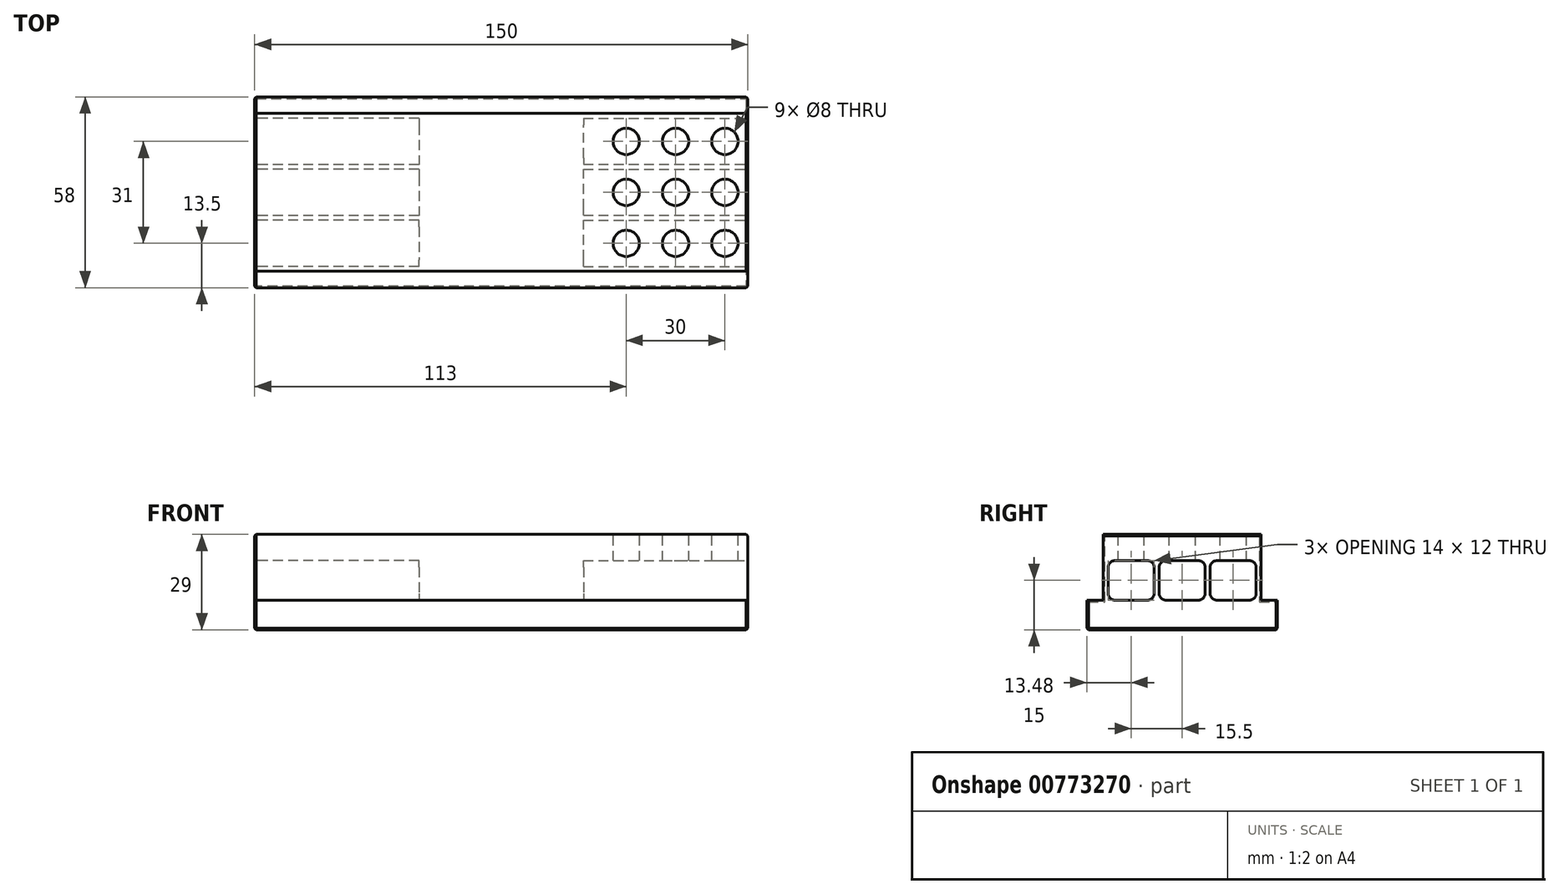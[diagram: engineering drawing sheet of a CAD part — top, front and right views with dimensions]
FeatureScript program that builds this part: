
annotation { "Feature Type Name" : "Feature", "Feature Type Description" : "" }
export const myFeature = defineFeature(function(context is Context, id is Id, definition is map)
    precondition{}
    {
        {
            var Q0;
            Q0=qCreatedBy(makeId("Top.planeOp"),FACE);
            var sketch = newSketch(context, id + "F0", { "sketchPlane" : qUnion([Q0])});
            skLineSegment(sketch, "E0.bottom", {"start": v(75, 29) * mm, "end": v(-75, 29) * mm});
            skLineSegment(sketch, "E0.top", {"start": v(75, -29) * mm, "end": v(-75, -29) * mm});
            skLineSegment(sketch, "E0.left", {"start": v(75, 29) * mm, "end": v(75, -29) * mm});
            skLineSegment(sketch, "E0.right", {"start": v(-75, 29) * mm, "end": v(-75, -29) * mm});
            skPoint(sketch, "E0.middle", {"position": v(0, 0) * mm});
            skSolve(sketch);
        }
        {
            var Q0;
            Q0 = qSketchRegion(id + "F0", true);
            extrude(context, id + "F1", {"entities" : qUnion([Q0]), "oppositeDirection" : true, "depth" : 29 * mm, "offsetDistance" : 25 * mm});
        }
        {
            var Q0;
            Q0=qCreatedBy(makeId("Top.planeOp"),FACE);
            var sketch = newSketch(context, id + "F2", { "sketchPlane" : qUnion([Q0])});
            skCircle(sketch, "E1", {"center": v(68, 15.5) * mm, "radius": 4 * mm});
            skCircle(sketch, "E2.0.1.0", {"center": v(68, 0) * mm, "radius": 4 * mm});
            skCircle(sketch, "E2.0.2.0", {"center": v(68, -15.5) * mm, "radius": 4 * mm});
            skCircle(sketch, "E2.1.0.0", {"center": v(53, 15.5) * mm, "radius": 4 * mm});
            skCircle(sketch, "E2.1.1.0", {"center": v(53, 0) * mm, "radius": 4 * mm});
            skCircle(sketch, "E2.1.2.0", {"center": v(53, -15.5) * mm, "radius": 4 * mm});
            skCircle(sketch, "E2.2.0.0", {"center": v(38, 15.5) * mm, "radius": 4 * mm});
            skCircle(sketch, "E2.2.1.0", {"center": v(38, 0) * mm, "radius": 4 * mm});
            skCircle(sketch, "E2.2.2.0", {"center": v(38, -15.5) * mm, "radius": 4 * mm});
            skLineSegment(sketch, "E2.direction1", {"start": v(68, 15.5) * mm, "end": v(53, 15.5) * mm, "construction": true});
            skLineSegment(sketch, "E2.direction2", {"start": v(68, 15.5) * mm, "end": v(68, 0) * mm, "construction": true});
            skLineSegment(sketch, "E3.MirrorCS", {"start": v(-68, 15.5) * mm, "end": v(-53, 15.5) * mm, "construction": true});
            skCircle(sketch, "E4.MirrorC", {"center": v(-53, 0) * mm, "radius": 4 * mm});
            skCircle(sketch, "E5.MirrorC", {"center": v(-53, 15.5) * mm, "radius": 4 * mm});
            skCircle(sketch, "E6.MirrorC", {"center": v(-53, -15.5) * mm, "radius": 4 * mm});
            skCircle(sketch, "E7.MirrorC", {"center": v(-68, 15.5) * mm, "radius": 4 * mm});
            skCircle(sketch, "E8.MirrorC", {"center": v(-38, 0) * mm, "radius": 4 * mm});
            skLineSegment(sketch, "E9.MirrorCS", {"start": v(-68, 15.5) * mm, "end": v(-68, 0) * mm, "construction": true});
            skCircle(sketch, "E10.MirrorC", {"center": v(-68, -15.5) * mm, "radius": 4 * mm});
            skCircle(sketch, "E11.MirrorC", {"center": v(-68, 0) * mm, "radius": 4 * mm});
            skCircle(sketch, "E12.MirrorC", {"center": v(-38, -15.5) * mm, "radius": 4 * mm});
            skCircle(sketch, "E13.MirrorC", {"center": v(-38, 15.5) * mm, "radius": 4 * mm});
            skSolve(sketch);
        }
        {
            var Q0;
            Q0=makeQuery(id+"F1.opExtrude","SWEPT_FACE",FACE,{"disambiguationData":[OSD([sQuery(id+"F0.wireOp",EDGE,"E0.left")])]});
            var sketch = newSketch(context, id + "F3", { "sketchPlane" : qUnion([Q0])});
            skLineSegment(sketch, "E14.bottom", {"start": v(-29, 0) * mm, "end": v(-24, 0) * mm});
            skLineSegment(sketch, "E14.top", {"start": v(-29, -20) * mm, "end": v(-24, -20) * mm});
            skLineSegment(sketch, "E14.left", {"start": v(-29, 0) * mm, "end": v(-29, -20) * mm});
            skLineSegment(sketch, "E14.right", {"start": v(-24, 0) * mm, "end": v(-24, -20) * mm});
            skLineSegment(sketch, "E15.bottom", {"start": v(29, 0) * mm, "end": v(24, 0) * mm});
            skLineSegment(sketch, "E15.top", {"start": v(29, -20) * mm, "end": v(24, -20) * mm});
            skLineSegment(sketch, "E15.left", {"start": v(29, 0) * mm, "end": v(29, -20) * mm});
            skLineSegment(sketch, "E15.right", {"start": v(24, 0) * mm, "end": v(24, -20) * mm});
            skSolve(sketch);
        }
        {
            var Q0;
            Q0=makeQuery(id+"F3.imprint","IMPRINT",FACE,{"disambiguationData":[TD([[makeQuery(id+"F3.imprint","IMPRINT",EDGE,{"derivedFrom":sQuery(id+"F3.wireOp",EDGE,"E14.bottom")}),1.0]])]});
            var Q1;
            Q1=makeQuery(id+"F3.imprint","IMPRINT",FACE,{"disambiguationData":[TD([[makeQuery(id+"F3.imprint","IMPRINT",EDGE,{"derivedFrom":sQuery(id+"F3.wireOp",EDGE,"E15.bottom")}),1.0]])]});
            extrude(context, id + "F4", {"entities" : qUnion([Q0, Q1]), "operationType" : NewBodyOperationType.REMOVE, "endBound" : BoundingType.THROUGH_ALL, "oppositeDirection" : true, "depth" : 25 * mm, "offsetDistance" : 25 * mm});
        }
        {
            var Q0;
            Q0=makeQuery(id+"F2.imprint","IMPRINT",FACE,{"disambiguationData":[TD([[makeQuery(id+"F2.imprint","IMPRINT",EDGE,{"derivedFrom":sQuery(id+"F2.wireOp",EDGE,"E1")}),1.0]])]});
            var Q1;
            Q1=makeQuery(id+"F2.imprint","IMPRINT",FACE,{"disambiguationData":[TD([[makeQuery(id+"F2.imprint","IMPRINT",EDGE,{"derivedFrom":sQuery(id+"F2.wireOp",EDGE,"E2.2.2.0")}),1.0]])]});
            var Q2;
            Q2=makeQuery(id+"F2.imprint","IMPRINT",FACE,{"disambiguationData":[TD([[makeQuery(id+"F2.imprint","IMPRINT",EDGE,{"derivedFrom":sQuery(id+"F2.wireOp",EDGE,"E2.2.0.0")}),1.0]])]});
            var Q3;
            Q3=makeQuery(id+"F2.imprint","IMPRINT",FACE,{"disambiguationData":[TD([[makeQuery(id+"F2.imprint","IMPRINT",EDGE,{"derivedFrom":sQuery(id+"F2.wireOp",EDGE,"E2.2.1.0")}),1.0]])]});
            var Q4;
            Q4=makeQuery(id+"F2.imprint","IMPRINT",FACE,{"disambiguationData":[TD([[makeQuery(id+"F2.imprint","IMPRINT",EDGE,{"derivedFrom":sQuery(id+"F2.wireOp",EDGE,"E2.0.1.0")}),1.0]])]});
            var Q5;
            Q5=makeQuery(id+"F2.imprint","IMPRINT",FACE,{"disambiguationData":[TD([[makeQuery(id+"F2.imprint","IMPRINT",EDGE,{"derivedFrom":sQuery(id+"F2.wireOp",EDGE,"E2.1.2.0")}),1.0]])]});
            var Q6;
            Q6=makeQuery(id+"F2.imprint","IMPRINT",FACE,{"disambiguationData":[TD([[makeQuery(id+"F2.imprint","IMPRINT",EDGE,{"derivedFrom":sQuery(id+"F2.wireOp",EDGE,"E2.0.2.0")}),1.0]])]});
            var Q7;
            Q7=makeQuery(id+"F2.imprint","IMPRINT",FACE,{"disambiguationData":[TD([[makeQuery(id+"F2.imprint","IMPRINT",EDGE,{"derivedFrom":sQuery(id+"F2.wireOp",EDGE,"E2.1.1.0")}),1.0]])]});
            var Q8;
            Q8=makeQuery(id+"F2.imprint","IMPRINT",FACE,{"disambiguationData":[TD([[makeQuery(id+"F2.imprint","IMPRINT",EDGE,{"derivedFrom":sQuery(id+"F2.wireOp",EDGE,"E2.1.0.0")}),1.0]])]});
            var Q9;
            Q9=makeQuery(id+"F2.imprint","IMPRINT",FACE,{"disambiguationData":[TD([[makeQuery(id+"F2.imprint","IMPRINT",EDGE,{"derivedFrom":sQuery(id+"F2.wireOp",EDGE,"E7.MirrorC")}),-1.0]])]});
            var Q10;
            Q10=makeQuery(id+"F2.imprint","IMPRINT",FACE,{"disambiguationData":[TD([[makeQuery(id+"F2.imprint","IMPRINT",EDGE,{"derivedFrom":sQuery(id+"F2.wireOp",EDGE,"E4.MirrorC")}),-1.0]])]});
            var Q11;
            Q11=makeQuery(id+"F2.imprint","IMPRINT",FACE,{"disambiguationData":[TD([[makeQuery(id+"F2.imprint","IMPRINT",EDGE,{"derivedFrom":sQuery(id+"F2.wireOp",EDGE,"E8.MirrorC")}),-1.0]])]});
            var Q12;
            Q12=makeQuery(id+"F2.imprint","IMPRINT",FACE,{"disambiguationData":[TD([[makeQuery(id+"F2.imprint","IMPRINT",EDGE,{"derivedFrom":sQuery(id+"F2.wireOp",EDGE,"E10.MirrorC")}),-1.0]])]});
            var Q13;
            Q13=makeQuery(id+"F2.imprint","IMPRINT",FACE,{"disambiguationData":[TD([[makeQuery(id+"F2.imprint","IMPRINT",EDGE,{"derivedFrom":sQuery(id+"F2.wireOp",EDGE,"E12.MirrorC")}),-1.0]])]});
            var Q14;
            Q14=makeQuery(id+"F2.imprint","IMPRINT",FACE,{"disambiguationData":[TD([[makeQuery(id+"F2.imprint","IMPRINT",EDGE,{"derivedFrom":sQuery(id+"F2.wireOp",EDGE,"E11.MirrorC")}),-1.0]])]});
            var Q15;
            Q15=makeQuery(id+"F2.imprint","IMPRINT",FACE,{"disambiguationData":[TD([[makeQuery(id+"F2.imprint","IMPRINT",EDGE,{"derivedFrom":sQuery(id+"F2.wireOp",EDGE,"E13.MirrorC")}),-1.0]])]});
            var Q16;
            Q16=makeQuery(id+"F2.imprint","IMPRINT",FACE,{"disambiguationData":[TD([[makeQuery(id+"F2.imprint","IMPRINT",EDGE,{"derivedFrom":sQuery(id+"F2.wireOp",EDGE,"E5.MirrorC")}),-1.0]])]});
            var Q17;
            Q17=makeQuery(id+"F2.imprint","IMPRINT",FACE,{"disambiguationData":[TD([[makeQuery(id+"F2.imprint","IMPRINT",EDGE,{"derivedFrom":sQuery(id+"F2.wireOp",EDGE,"E6.MirrorC")}),-1.0]])]});
            extrude(context, id + "F5", {"entities" : qUnion([Q0, Q1, Q2, Q3, Q4, Q5, Q6, Q7, Q8, Q9, Q10, Q11, Q12, Q13, Q14, Q15, Q16, Q17]), "operationType" : NewBodyOperationType.REMOVE, "oppositeDirection" : true, "depth" : 20 * mm, "offsetDistance" : 25 * mm});
        }
        {
            var Q0;
            Q0=makeQuery(id+"F1.opExtrude","SWEPT_FACE",FACE,{"disambiguationData":[OSD([sQuery(id+"F0.wireOp",EDGE,"E0.left")])]});
            var sketch = newSketch(context, id + "F6", { "sketchPlane" : qUnion([Q0])});
            skLineSegment(sketch, "E16.bottom", {"start": v(-20.5, -8) * mm, "end": v(-10.5, -8) * mm});
            skLineSegment(sketch, "E16.top", {"start": v(-20.5, -20) * mm, "end": v(-10.5, -20) * mm});
            skLineSegment(sketch, "E16.left", {"start": v(-22.5, -10) * mm, "end": v(-22.5, -18) * mm});
            skLineSegment(sketch, "E16.right", {"start": v(-8.5, -10) * mm, "end": v(-8.5, -18) * mm});
            skLineSegment(sketch, "E17.1.0.0", {"start": v(7, -10) * mm, "end": v(7, -18) * mm});
            skLineSegment(sketch, "E17.1.0.1", {"start": v(-5, -8) * mm, "end": v(5, -8) * mm});
            skLineSegment(sketch, "E17.1.0.2", {"start": v(-7, -10) * mm, "end": v(-7, -18) * mm});
            skLineSegment(sketch, "E17.1.0.3", {"start": v(-5, -20) * mm, "end": v(5, -20) * mm});
            skLineSegment(sketch, "E17.2.0.0", {"start": v(22.5, -10) * mm, "end": v(22.5, -18) * mm});
            skLineSegment(sketch, "E17.2.0.1", {"start": v(10.5, -8) * mm, "end": v(20.5, -8) * mm});
            skLineSegment(sketch, "E17.2.0.2", {"start": v(8.5, -10) * mm, "end": v(8.5, -18) * mm});
            skLineSegment(sketch, "E17.2.0.3", {"start": v(10.5, -20) * mm, "end": v(20.5, -20) * mm});
            skLineSegment(sketch, "E17.direction1", {"start": v(-8.5, -20) * mm, "end": v(7, -20) * mm, "construction": true});
            skLineSegment(sketch, "E18", {"start": v(0, -8) * mm, "end": v(0, -20) * mm, "construction": true});
            skPoint(sketch, "E19.visualSharp", {"position": v(-22.5, -8) * mm});
            skArc(sketch, "E19.filletArc", {"start": v(-20.5, -8) * mm, "mid": v(-21.91, -8.59) * mm, "end": v(-22.5, -10) * mm});
            skPoint(sketch, "E20.visualSharp", {"position": v(-22.5, -20) * mm});
            skArc(sketch, "E20.filletArc", {"start": v(-22.5, -18) * mm, "mid": v(-21.91, -19.41) * mm, "end": v(-20.5, -20) * mm});
            skPoint(sketch, "E21.visualSharp", {"position": v(-8.5, -20) * mm});
            skArc(sketch, "E21.filletArc", {"start": v(-10.5, -20) * mm, "mid": v(-9.09, -19.41) * mm, "end": v(-8.5, -18) * mm});
            skPoint(sketch, "E22.visualSharp", {"position": v(-8.5, -8) * mm});
            skArc(sketch, "E22.filletArc", {"start": v(-8.5, -10) * mm, "mid": v(-9.09, -8.59) * mm, "end": v(-10.5, -8) * mm});
            skPoint(sketch, "E23.visualSharp", {"position": v(-7, -8) * mm});
            skArc(sketch, "E23.filletArc", {"start": v(-5, -8) * mm, "mid": v(-6.41, -8.59) * mm, "end": v(-7, -10) * mm});
            skPoint(sketch, "E24.visualSharp", {"position": v(-7, -20) * mm});
            skArc(sketch, "E24.filletArc", {"start": v(-7, -18) * mm, "mid": v(-6.41, -19.41) * mm, "end": v(-5, -20) * mm});
            skPoint(sketch, "E25.visualSharp", {"position": v(7, -20) * mm});
            skArc(sketch, "E25.filletArc", {"start": v(5, -20) * mm, "mid": v(6.41, -19.41) * mm, "end": v(7, -18) * mm});
            skPoint(sketch, "E26.visualSharp", {"position": v(7, -8) * mm});
            skArc(sketch, "E26.filletArc", {"start": v(7, -10) * mm, "mid": v(6.41, -8.59) * mm, "end": v(5, -8) * mm});
            skPoint(sketch, "E27.visualSharp", {"position": v(8.5, -8) * mm});
            skArc(sketch, "E27.filletArc", {"start": v(10.5, -8) * mm, "mid": v(9.09, -8.59) * mm, "end": v(8.5, -10) * mm});
            skPoint(sketch, "E28.visualSharp", {"position": v(22.5, -20) * mm});
            skArc(sketch, "E28.filletArc", {"start": v(20.5, -20) * mm, "mid": v(21.91, -19.41) * mm, "end": v(22.5, -18) * mm});
            skPoint(sketch, "E29.visualSharp", {"position": v(22.5, -8) * mm});
            skArc(sketch, "E29.filletArc", {"start": v(22.5, -10) * mm, "mid": v(21.91, -8.59) * mm, "end": v(20.5, -8) * mm});
            skPoint(sketch, "E30.visualSharp", {"position": v(8.5, -20) * mm});
            skArc(sketch, "E30.filletArc", {"start": v(8.5, -18) * mm, "mid": v(9.09, -19.41) * mm, "end": v(10.5, -20) * mm});
            skSolve(sketch);
        }
        {
            var Q0;
            Q0=makeQuery(id+"F1.opExtrude","SWEPT_FACE",FACE,{"disambiguationData":[OSD([sQuery(id+"F0.wireOp",EDGE,"E0.right")])]});
            var sketch = newSketch(context, id + "F7", { "sketchPlane" : qUnion([Q0])});
            skLineSegment(sketch, "E31.bottom", {"start": v(-20.48, -8) * mm, "end": v(-10.48, -8) * mm});
            skLineSegment(sketch, "E31.top", {"start": v(-20.48, -20) * mm, "end": v(-10.48, -20) * mm});
            skLineSegment(sketch, "E31.left", {"start": v(-22.48, -10) * mm, "end": v(-22.48, -18) * mm});
            skLineSegment(sketch, "E31.right", {"start": v(-8.48, -10) * mm, "end": v(-8.48, -18) * mm});
            skLineSegment(sketch, "E32.1.0.0", {"start": v(7.02, -10) * mm, "end": v(7.02, -18) * mm});
            skLineSegment(sketch, "E32.1.0.1", {"start": v(-4.98, -8) * mm, "end": v(5.02, -8) * mm});
            skLineSegment(sketch, "E32.1.0.2", {"start": v(-6.98, -10) * mm, "end": v(-6.98, -18) * mm});
            skLineSegment(sketch, "E32.1.0.3", {"start": v(-4.98, -20) * mm, "end": v(5.02, -20) * mm});
            skLineSegment(sketch, "E32.2.0.0", {"start": v(22.52, -10) * mm, "end": v(22.52, -18) * mm});
            skLineSegment(sketch, "E32.2.0.1", {"start": v(10.52, -8) * mm, "end": v(20.52, -8) * mm});
            skLineSegment(sketch, "E32.2.0.2", {"start": v(8.52, -10) * mm, "end": v(8.52, -18) * mm});
            skLineSegment(sketch, "E32.2.0.3", {"start": v(10.52, -20) * mm, "end": v(20.52, -20) * mm});
            skLineSegment(sketch, "E32.direction1", {"start": v(-8.48, -20) * mm, "end": v(7.02, -20) * mm, "construction": true});
            skLineSegment(sketch, "E33", {"start": v(0.02, -8) * mm, "end": v(0.02, -20) * mm, "construction": true});
            skPoint(sketch, "E34.visualSharp", {"position": v(-22.48, -8) * mm});
            skArc(sketch, "E34.filletArc", {"start": v(-20.48, -8) * mm, "mid": v(-21.9, -8.59) * mm, "end": v(-22.48, -10) * mm});
            skPoint(sketch, "E35.visualSharp", {"position": v(-22.48, -20) * mm});
            skArc(sketch, "E35.filletArc", {"start": v(-22.48, -18) * mm, "mid": v(-21.9, -19.41) * mm, "end": v(-20.48, -20) * mm});
            skPoint(sketch, "E36.visualSharp", {"position": v(-8.48, -20) * mm});
            skArc(sketch, "E36.filletArc", {"start": v(-10.48, -20) * mm, "mid": v(-9.07, -19.41) * mm, "end": v(-8.48, -18) * mm});
            skPoint(sketch, "E37.visualSharp", {"position": v(-8.48, -8) * mm});
            skArc(sketch, "E37.filletArc", {"start": v(-8.48, -10) * mm, "mid": v(-9.07, -8.59) * mm, "end": v(-10.48, -8) * mm});
            skPoint(sketch, "E38.visualSharp", {"position": v(-6.98, -8) * mm});
            skArc(sketch, "E38.filletArc", {"start": v(-4.98, -8) * mm, "mid": v(-6.4, -8.59) * mm, "end": v(-6.98, -10) * mm});
            skPoint(sketch, "E39.visualSharp", {"position": v(-6.98, -20) * mm});
            skArc(sketch, "E39.filletArc", {"start": v(-6.98, -18) * mm, "mid": v(-6.4, -19.41) * mm, "end": v(-4.98, -20) * mm});
            skPoint(sketch, "E40.visualSharp", {"position": v(7.02, -20) * mm});
            skArc(sketch, "E40.filletArc", {"start": v(5.02, -20) * mm, "mid": v(6.43, -19.41) * mm, "end": v(7.02, -18) * mm});
            skPoint(sketch, "E41.visualSharp", {"position": v(7.02, -8) * mm});
            skArc(sketch, "E41.filletArc", {"start": v(7.02, -10) * mm, "mid": v(6.43, -8.59) * mm, "end": v(5.02, -8) * mm});
            skPoint(sketch, "E42.visualSharp", {"position": v(8.52, -8) * mm});
            skArc(sketch, "E42.filletArc", {"start": v(10.52, -8) * mm, "mid": v(9.1, -8.59) * mm, "end": v(8.52, -10) * mm});
            skPoint(sketch, "E43.visualSharp", {"position": v(22.52, -20) * mm});
            skArc(sketch, "E43.filletArc", {"start": v(20.52, -20) * mm, "mid": v(21.93, -19.41) * mm, "end": v(22.52, -18) * mm});
            skPoint(sketch, "E44.visualSharp", {"position": v(22.52, -8) * mm});
            skArc(sketch, "E44.filletArc", {"start": v(22.52, -10) * mm, "mid": v(21.93, -8.59) * mm, "end": v(20.52, -8) * mm});
            skPoint(sketch, "E45.visualSharp", {"position": v(8.52, -20) * mm});
            skArc(sketch, "E45.filletArc", {"start": v(8.52, -18) * mm, "mid": v(9.1, -19.41) * mm, "end": v(10.52, -20) * mm});
            skSolve(sketch);
        }
        {
            var Q0;
            Q0=makeQuery(id+"F6.imprint","IMPRINT",FACE,{"disambiguationData":[TD([[makeQuery(id+"F6.imprint","IMPRINT",EDGE,{"derivedFrom":sQuery(id+"F6.wireOp",EDGE,"E16.bottom")}),-1.0]])]});
            var Q1;
            Q1=makeQuery(id+"F6.imprint","IMPRINT",FACE,{"disambiguationData":[TD([[makeQuery(id+"F6.imprint","IMPRINT",EDGE,{"derivedFrom":sQuery(id+"F6.wireOp",EDGE,"E17.1.0.0")}),-1.0]])]});
            var Q2;
            Q2=makeQuery(id+"F6.imprint","IMPRINT",FACE,{"disambiguationData":[TD([[makeQuery(id+"F6.imprint","IMPRINT",EDGE,{"derivedFrom":sQuery(id+"F6.wireOp",EDGE,"E17.2.0.0")}),-1.0]])]});
            extrude(context, id + "F8", {"entities" : qUnion([Q0, Q1, Q2]), "operationType" : NewBodyOperationType.REMOVE, "oppositeDirection" : true, "depth" : 50 * mm, "offsetDistance" : 25 * mm});
        }
        {
            var Q0;
            Q0=makeQuery(id+"F7.imprint","IMPRINT",FACE,{"disambiguationData":[TD([[makeQuery(id+"F7.imprint","IMPRINT",EDGE,{"derivedFrom":sQuery(id+"F7.wireOp",EDGE,"E31.bottom")}),-1.0]])]});
            var Q1;
            Q1=makeQuery(id+"F7.imprint","IMPRINT",FACE,{"disambiguationData":[TD([[makeQuery(id+"F7.imprint","IMPRINT",EDGE,{"derivedFrom":sQuery(id+"F7.wireOp",EDGE,"E32.1.0.0")}),-1.0]])]});
            var Q2;
            Q2=makeQuery(id+"F7.imprint","IMPRINT",FACE,{"disambiguationData":[TD([[makeQuery(id+"F7.imprint","IMPRINT",EDGE,{"derivedFrom":sQuery(id+"F7.wireOp",EDGE,"E32.2.0.0")}),-1.0]])]});
            extrude(context, id + "F9", {"entities" : qUnion([Q0, Q1, Q2]), "operationType" : NewBodyOperationType.REMOVE, "oppositeDirection" : true, "depth" : 50 * mm, "offsetDistance" : 25 * mm});
        }
        {
            var Q0;
            Q0=makeQuery(id+"F8.boolean.opBoolean","COPY",EDGE,{"derivedFrom":makeQuery(id+"F8.opExtrude","CAP_EDGE",EDGE,{"disambiguationData":[OSD([sQuery(id+"F6.wireOp",EDGE,"E16.bottom")])],"isStart":true})});
            var Q1;
            Q1=makeQuery(id+"F8.boolean.opBoolean","COPY",EDGE,{"derivedFrom":makeQuery(id+"F8.opExtrude","CAP_EDGE",EDGE,{"disambiguationData":[OSD([sQuery(id+"F6.wireOp",EDGE,"E17.1.0.1")])],"isStart":true})});
            var Q2;
            Q2=makeQuery(id+"F8.boolean.opBoolean","COPY",EDGE,{"derivedFrom":makeQuery(id+"F8.opExtrude","CAP_EDGE",EDGE,{"disambiguationData":[OSD([sQuery(id+"F6.wireOp",EDGE,"E17.2.0.1")])],"isStart":true})});
            var Q3;
            Q3=makeQuery(id+"F9.boolean.opBoolean","COPY",EDGE,{"derivedFrom":makeQuery(id+"F9.opExtrude","CAP_EDGE",EDGE,{"disambiguationData":[OSD([sQuery(id+"F7.wireOp",EDGE,"E31.bottom")])],"isStart":true})});
            var Q4;
            Q4=makeQuery(id+"F9.boolean.opBoolean","COPY",EDGE,{"derivedFrom":makeQuery(id+"F9.opExtrude","CAP_EDGE",EDGE,{"disambiguationData":[OSD([sQuery(id+"F7.wireOp",EDGE,"E32.1.0.1")])],"isStart":true})});
            var Q5;
            Q5=makeQuery(id+"F9.boolean.opBoolean","COPY",EDGE,{"derivedFrom":makeQuery(id+"F9.opExtrude","CAP_EDGE",EDGE,{"disambiguationData":[OSD([sQuery(id+"F7.wireOp",EDGE,"E32.2.0.1")])],"isStart":true})});
            var Q6;
            Q6=makeQuery(id+"F4.boolean.opBoolean","COPY",EDGE,{"derivedFrom":makeQuery(id+"F4.opExtrude","CAP_EDGE",EDGE,{"disambiguationData":[OSD([sQuery(id+"F3.wireOp",EDGE,"E14.right")])],"isStart":true})});
            var Q7;
            Q7=makeQuery(id+"F1.opExtrude","CAP_EDGE",EDGE,{"disambiguationData":[OSD([sQuery(id+"F0.wireOp",EDGE,"E0.left")])],"isStart":true});
            var Q8;
            Q8=makeQuery(id+"F4.boolean.opBoolean","COPY",EDGE,{"derivedFrom":makeQuery(id+"F4.opExtrude","CAP_EDGE",EDGE,{"disambiguationData":[OSD([sQuery(id+"F3.wireOp",EDGE,"E15.right")])],"isStart":true})});
            var Q9;
            Q9=makeQuery(id+"F4.boolean.opBoolean","COPY",EDGE,{"derivedFrom":makeQuery(id+"F4.opExtrude","SWEPT_EDGE",EDGE,{"disambiguationData":[OSD([sQuery(id+"F0.wireOp",EDGE,"E0.left"),sQuery(id+"F3.wireOp",EDGE,"E14.bottom"),sQuery(id+"F3.wireOp",EDGE,"E14.right")])]})});
            var Q10;
            Q10=makeQuery(id+"F4.boolean.opBoolean","COPY",EDGE,{"derivedFrom":makeQuery(id+"F4.opExtrude","SWEPT_EDGE",EDGE,{"disambiguationData":[OSD([sQuery(id+"F0.wireOp",EDGE,"E0.left"),sQuery(id+"F3.wireOp",EDGE,"E15.bottom"),sQuery(id+"F3.wireOp",EDGE,"E15.right")])]})});
            var Q11;
            Q11=makeQuery(id+"F1.opExtrude","CAP_EDGE",EDGE,{"disambiguationData":[OSD([sQuery(id+"F0.wireOp",EDGE,"E0.right")])],"isStart":true});
            var Q12;
            Q12=makeQuery(id+"F4.boolean.opBoolean","INTERSECT",EDGE,{"derivedFrom":[makeQuery(id+"F1.opExtrude","SWEPT_FACE",FACE,{"disambiguationData":[OSD([sQuery(id+"F0.wireOp",EDGE,"E0.right")])]}),makeQuery(id+"F4.opExtrude","SWEPT_FACE",FACE,{"disambiguationData":[OSD([sQuery(id+"F3.wireOp",EDGE,"E15.right")])]})]});
            var Q13;
            Q13=makeQuery(id+"F4.boolean.opBoolean","INTERSECT",EDGE,{"derivedFrom":[makeQuery(id+"F1.opExtrude","SWEPT_FACE",FACE,{"disambiguationData":[OSD([sQuery(id+"F0.wireOp",EDGE,"E0.right")])]}),makeQuery(id+"F4.opExtrude","SWEPT_FACE",FACE,{"disambiguationData":[OSD([sQuery(id+"F3.wireOp",EDGE,"E14.right")])]})]});
            var Q14;
            Q14=makeQuery(id+"F4.boolean.opBoolean","COPY",EDGE,{"derivedFrom":makeQuery(id+"F4.opExtrude","CAP_EDGE",EDGE,{"disambiguationData":[OSD([sQuery(id+"F3.wireOp",EDGE,"E14.top")])],"isStart":true})});
            var Q15;
            Q15=makeQuery(id+"F4.boolean.opBoolean","COPY",EDGE,{"derivedFrom":makeQuery(id+"F4.opExtrude","SWEPT_EDGE",EDGE,{"disambiguationData":[OSD([sQuery(id+"F0.wireOp",EDGE,"E0.top"),sQuery(id+"F0.wireOp",EDGE,"E0.left"),sQuery(id+"F3.wireOp",EDGE,"E14.top"),sQuery(id+"F3.wireOp",EDGE,"E14.left")])]})});
            var Q16;
            Q16=makeQuery(id+"F4.boolean.opBoolean","INTERSECT",EDGE,{"derivedFrom":[makeQuery(id+"F1.opExtrude","SWEPT_FACE",FACE,{"disambiguationData":[OSD([sQuery(id+"F0.wireOp",EDGE,"E0.right")])]}),makeQuery(id+"F4.opExtrude","SWEPT_FACE",FACE,{"disambiguationData":[OSD([sQuery(id+"F3.wireOp",EDGE,"E14.top")])]})]});
            var Q17;
            Q17=makeQuery(id+"F4.boolean.opBoolean","COPY",EDGE,{"derivedFrom":makeQuery(id+"F4.opExtrude","CAP_EDGE",EDGE,{"disambiguationData":[OSD([sQuery(id+"F3.wireOp",EDGE,"E15.top")])],"isStart":true})});
            var Q18;
            Q18=makeQuery(id+"F4.boolean.opBoolean","COPY",EDGE,{"derivedFrom":makeQuery(id+"F4.opExtrude","SWEPT_EDGE",EDGE,{"disambiguationData":[OSD([sQuery(id+"F0.wireOp",EDGE,"E0.bottom"),sQuery(id+"F0.wireOp",EDGE,"E0.left"),sQuery(id+"F3.wireOp",EDGE,"E15.top"),sQuery(id+"F3.wireOp",EDGE,"E15.left")])]})});
            var Q19;
            Q19=makeQuery(id+"F4.boolean.opBoolean","INTERSECT",EDGE,{"derivedFrom":[makeQuery(id+"F1.opExtrude","SWEPT_FACE",FACE,{"disambiguationData":[OSD([sQuery(id+"F0.wireOp",EDGE,"E0.right")])]}),makeQuery(id+"F4.opExtrude","SWEPT_FACE",FACE,{"disambiguationData":[OSD([sQuery(id+"F3.wireOp",EDGE,"E15.top")])]})]});
            var Q20;
            Q20=makeQuery(id+"F1.opExtrude","SWEPT_EDGE",EDGE,{"disambiguationData":[OSD([sQuery(id+"F0.wireOp",EDGE,"E0.bottom"),sQuery(id+"F0.wireOp",EDGE,"E0.left")])]});
            var Q21;
            Q21=makeQuery(id+"F1.opExtrude","SWEPT_EDGE",EDGE,{"disambiguationData":[OSD([sQuery(id+"F0.wireOp",EDGE,"E0.top"),sQuery(id+"F0.wireOp",EDGE,"E0.left")])]});
            var Q22;
            Q22=makeQuery(id+"F1.opExtrude","SWEPT_EDGE",EDGE,{"disambiguationData":[OSD([sQuery(id+"F0.wireOp",EDGE,"E0.bottom"),sQuery(id+"F0.wireOp",EDGE,"E0.right")])]});
            var Q23;
            Q23=makeQuery(id+"F1.opExtrude","SWEPT_EDGE",EDGE,{"disambiguationData":[OSD([sQuery(id+"F0.wireOp",EDGE,"E0.top"),sQuery(id+"F0.wireOp",EDGE,"E0.right")])]});
            var Q24;
            Q24=makeQuery(id+"F1.opExtrude","CAP_EDGE",EDGE,{"disambiguationData":[OSD([sQuery(id+"F0.wireOp",EDGE,"E0.top")])],"isStart":false});
            var Q25;
            Q25=makeQuery(id+"F1.opExtrude","CAP_EDGE",EDGE,{"disambiguationData":[OSD([sQuery(id+"F0.wireOp",EDGE,"E0.right")])],"isStart":false});
            var Q26;
            Q26=makeQuery(id+"F1.opExtrude","CAP_EDGE",EDGE,{"disambiguationData":[OSD([sQuery(id+"F0.wireOp",EDGE,"E0.left")])],"isStart":false});
            var Q27;
            Q27=makeQuery(id+"F1.opExtrude","CAP_EDGE",EDGE,{"disambiguationData":[OSD([sQuery(id+"F0.wireOp",EDGE,"E0.bottom")])],"isStart":false});
            chamfer(context, id + "F10", {"entities" : qUnion([Q0, Q1, Q2, Q3, Q4, Q5, Q6, Q7, Q8, Q9, Q10, Q11, Q12, Q13, Q14, Q15, Q16, Q17, Q18, Q19, Q20, Q21, Q22, Q23, Q24, Q25, Q26, Q27]), "width" : 0.5 * mm, "tangentPropagation" : true});
        }
    });
